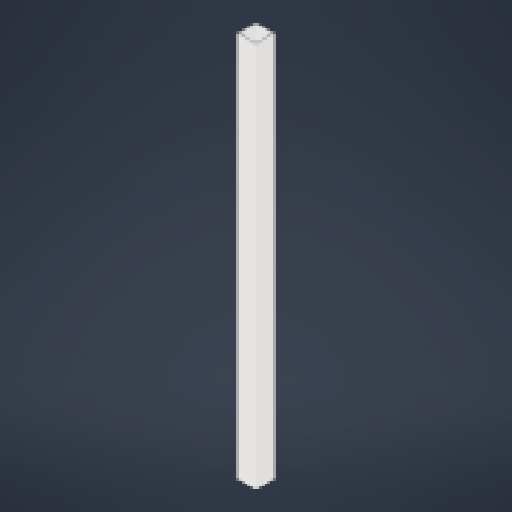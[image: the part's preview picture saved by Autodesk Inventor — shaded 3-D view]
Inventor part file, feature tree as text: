
AUTODESK INVENTOR PART (.ipt)
format: ipt  version: 2024 (Build 280153000, 153)  size: 139,264 bytes
history: native  units: mm
features: other x2, extrude x1, sketch x1
ambient origin geometry x8: Origin, YZ Plane, XZ Plane, XY Plane, X Axis, Y Axis, Z Axis, Center Point
bodies: Body1 (feature_tree)
feature tree (4):
  other  "Твердое тело1"
  other  "РабПлоскость2"
  extrude  "Выдавливание1"  Depth=20.0mm
  sketch  "Эскиз1"
